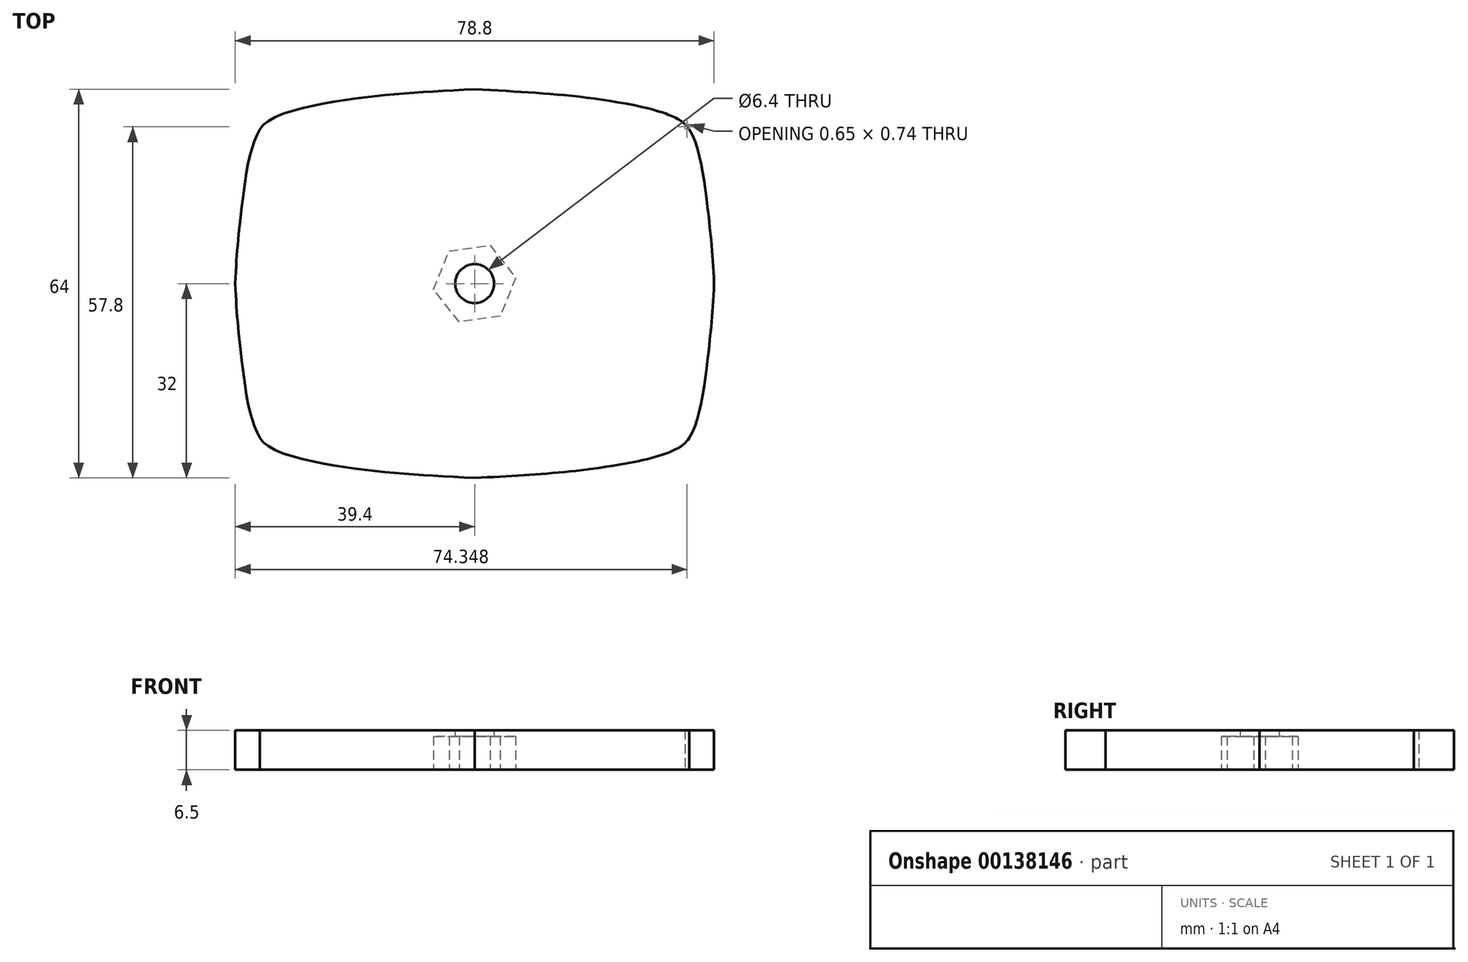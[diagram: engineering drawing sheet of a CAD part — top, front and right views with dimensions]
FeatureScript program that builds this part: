
annotation { "Feature Type Name" : "Feature", "Feature Type Description" : "" }
export const myFeature = defineFeature(function(context is Context, id is Id, definition is map)
    precondition{}
    {
        {
            var Q0;
            Q0=qCreatedBy(makeId("Top.planeOp"),FACE);
            var sketch = newSketch(context, id + "F0", { "sketchPlane" : qUnion([Q0])});
            skPoint(sketch, "E0.middle", {"position": v(0, 0) * mm});
            skLineSegment(sketch, "E1", {"start": v(16.45, 30.83) * mm, "end": v(16.45, 31) * mm, "construction": true});
            skLineSegment(sketch, "E2", {"start": v(28.79, 28.77) * mm, "end": v(28.79, 29) * mm});
            skArc(sketch, "E3", {"start": v(35.39, 25.22) * mm, "mid": v(35.06, 25.74) * mm, "end": v(34.62, 26.17) * mm});
            skFitSpline(sketch, "E4.MirrorCS", {"points": [v(39.4, 0) * mm, v(38.4, -12) * mm, v(32.9, -26.69) * mm], "startDerivative": vector(-1.08, -27.51) * mm, "endDerivative": vector(-20.82, 3.63) * mm});
            skFitSpline(sketch, "E5.MirrorCS", {"points": [v(0, -32.5) * mm, v(22.62, -30) * mm, v(35.5, -24) * mm], "startDerivative": vector(44.2, 2.69) * mm, "endDerivative": vector(-4.78, 22.64) * mm});
            skFitSpline(sketch, "E6.MirrorCS", {"points": [v(0, -32) * mm, v(22.62, -30) * mm, v(35.5, -24) * mm], "startDerivative": vector(44.2, 2.69) * mm, "endDerivative": vector(-4.78, 22.64) * mm});
            skFitSpline(sketch, "E7.MirrorCS", {"points": [v(0, -32) * mm, v(-22.62, -30) * mm, v(-35.5, -24) * mm], "startDerivative": vector(-44.2, 2.69) * mm, "endDerivative": vector(4.78, 22.64) * mm});
            skFitSpline(sketch, "E8.MirrorCS", {"points": [v(-39.4, 0) * mm, v(-38.4, -12) * mm, v(-32.9, -26.69) * mm], "startDerivative": vector(1.08, -27.51) * mm, "endDerivative": vector(20.82, 3.63) * mm});
            skCircle(sketch, "E9", {"center": v(0, 0) * mm, "radius": 3.2 * mm});
            skFitSpline(sketch, "E10.MirrorCS", {"points": [v(-39.4, 0) * mm, v(-38.4, 12) * mm, v(-32.9, 26.69) * mm], "startDerivative": vector(1.08, 27.51) * mm, "endDerivative": vector(20.82, -3.63) * mm});
            skFitSpline(sketch, "E11.MirrorCS", {"points": [v(0, 32) * mm, v(-22.62, 30) * mm, v(-35.5, 24) * mm], "startDerivative": vector(-44.2, -2.69) * mm, "endDerivative": vector(4.78, -22.64) * mm});
            skFitSpline(sketch, "E12.MirrorCS", {"points": [v(0, 32) * mm, v(22.62, 30) * mm, v(35.5, 24) * mm], "startDerivative": vector(44.2, -2.69) * mm, "endDerivative": vector(-4.78, -22.64) * mm});
            skFitSpline(sketch, "E13.MirrorCS", {"points": [v(39.4, 0) * mm, v(38.4, 12) * mm, v(32.9, 26.69) * mm], "startDerivative": vector(-1.08, 27.51) * mm, "endDerivative": vector(-20.82, -3.63) * mm});
            skSolve(sketch);
        }
        {
            var Q0;
            Q0 = qSketchRegion(id + "F0", true);
            extrude(context, id + "F1", {"entities" : qUnion([Q0]), "depth" : 6.5 * mm});
        }
        {
            var Q0;
            Q0=qCreatedBy(makeId("Top.planeOp"),FACE);
            var sketch = newSketch(context, id + "F2", { "sketchPlane" : qUnion([Q0])});
            skCircle(sketch, "E14.cCircle", {"center": v(0, 0) * mm, "radius": 6.82 * mm, "construction": true});
            skLineSegment(sketch, "E14.0", {"start": v(4.2, -5.37) * mm, "end": v(-2.55, -6.32) * mm});
            skLineSegment(sketch, "E14.1", {"start": v(-2.55, -6.32) * mm, "end": v(-6.75, -0.95) * mm});
            skLineSegment(sketch, "E14.2", {"start": v(-6.75, -0.95) * mm, "end": v(-4.2, 5.37) * mm});
            skLineSegment(sketch, "E14.3", {"start": v(-4.2, 5.37) * mm, "end": v(2.55, 6.32) * mm});
            skLineSegment(sketch, "E14.4", {"start": v(2.55, 6.32) * mm, "end": v(6.75, 0.95) * mm});
            skLineSegment(sketch, "E14.5", {"start": v(6.75, 0.95) * mm, "end": v(4.2, -5.37) * mm});
            skSolve(sketch);
        }
        {
            var Q0;
            Q0 = qSketchRegion(id + "F2", true);
            extrude(context, id + "F3", {"entities" : qUnion([Q0]), "operationType" : NewBodyOperationType.REMOVE, "depth" : 5.5 * mm});
        }
    });
